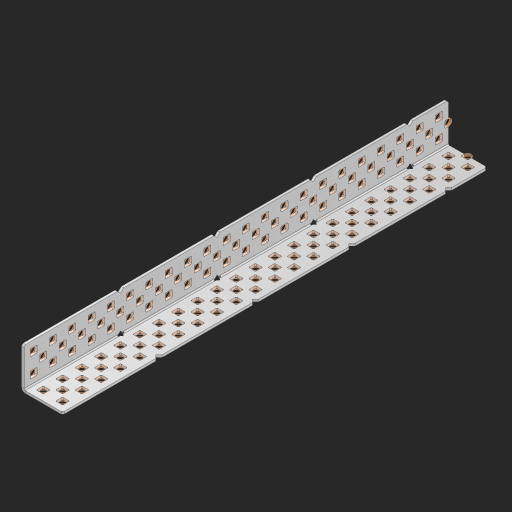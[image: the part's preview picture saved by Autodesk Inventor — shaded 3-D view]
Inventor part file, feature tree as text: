
AUTODESK INVENTOR PART (.ipt)
format: ipt  version: 2023 (Build 270158000, 158)  size: 1,655,808 bytes
history: native  units: in
note: dims shown in document units (in); Inventor stores cm internally (conversion verified against a paired STEP export)
features: other x138, extrude x130, sheet_metal_op x8, sketch x7, pattern_linear x2, mirror x1, chamfer x1
ambient origin geometry x8: Origin, YZ Plane, XZ Plane, XY Plane, X Axis, Y Axis, Z Axis, Center Point
bodies: Solid1 (feature_tree), Body (feature_tree)
feature tree (287):
  sheet_metal_op  "Flanges"
  sheet_metal_op  "Body Pattern"
  pattern_linear  "Center Pattern"  Spacing1=1.0in  [1 undecoded]
  other  "Arc Length"
  pattern_linear  "Notch Pattern"  Spacing1=0.25in  [1 undecoded]
  other  "Diagonal Plane"
  mirror  "Everything Mirrored"
  chamfer  "End Chamfer"
  sketch  "Sketch1"  dims[d0=1.0in]
  other  "Plate1"
  sketch  "Sketch2"  dims[d1=11.0in]
  other  "Plate2"
  sheet_metal_op  "Bend1"
  sheet_metal_op  "Corner1"
  sketch  "Sketch8"  dims[d2=0.0625in]
  sketch  "Sketch9"  dims[d3=0.0625in]
  other  "Srf91"
  sheet_metal_op  "Body Pattern Sketch"
  other  "Srf92"
  sketch  "Sketch13"  dims[d4=0.0312in]
  sketch  "Sketch15"  dims[d5=0.125in]
  sketch  "Sketch16"  dims[d6=0.0625in d7=1.0in d8=90.0deg d9=0.0312in d10=0.25in d11=0.0625in d12=0.0625in d49=0.182in d50=0.02in d52=0.25in d53=0.0625in d54=0.0in d55=0.172in d56=1.0in d57=0.0in d60=8.6614in d62=0.5in d63=0.7874in d65=0.5in d85=0.1473in d86=0.1782in d89=0.0625in d90=0.0in d91=0.04in d92=0.0491in d95=2.5in d96=0.04in d97=0.25in d98=45.0deg d99=0.25in d106=0.182in d107=0.02in d108=0.5in d110=0.0625in d111=0.0in d112=0.172in d113=0.5in d114=0.0in d117=0.5in d123=0.25in d125=0.25in d126=0.0491in d127=0.1473in d128=0.08in d129=0.04in d130=2.5in]
  other  "Srf786"
  other  "Srf856"
  other  "Srf857"
  other  "Srf858"
  other  "Srf859"
  other  "Srf860"
  other  "Srf861"
  other  "Srf889"
  other  "Srf890"
  other  "Srf891"
  other  "Srf1275"
  other  "Srf1276"
  other  "Srf1278"
  other  "Srf1279"
  other  "Srf1280"
  other  "Srf1281"
  other  "Srf1282"
  other  "Srf1283"
  other  "Srf1277"
  other  "Srf1285"
  other  "Srf1286"
  other  "Srf1287"
  other  "Srf1383"
  other  "Srf1384"
  other  "Srf1385"
  other  "Srf1386"
  other  "Srf1387"
  other  "Srf1388"
  other  "Srf1389"
  other  "Srf1390"
  other  "Srf1391"
  other  "Srf1392"
  other  "Srf1393"
  other  "Srf1394"
  other  "Srf1395"
  other  "Srf1396"
  other  "Srf1397"
  other  "Srf1398"
  other  "Srf1399"
  other  "Srf1400"
  other  "Srf1401"
  other  "Srf1402"
  other  "Srf1403"
  other  "Srf1404"
  other  "Srf1405"
  other  "Srf1406"
  other  "Srf1407"
  other  "Srf1408"
  other  "Srf1409"
  other  "Srf1410"
  other  "Srf1411"
  other  "Srf1412"
  other  "Srf1413"
  other  "Srf1414"
  other  "Srf1415"
  other  "Srf1416"
  other  "Srf1417"
  other  "Srf1418"
  other  "Srf1445"
  other  "Srf1446"
  other  "Srf1447"
  other  "Srf1448"
  other  "Srf1449"
  other  "Srf1450"
  other  "Srf1451"
  other  "Srf1452"
  other  "Srf1453"
  other  "Srf1454"
  other  "Srf1455"
  other  "Srf1456"
  other  "Srf1457"
  other  "Srf1458"
  other  "Srf1459"
  other  "Srf1460"
  other  "Srf1461"
  other  "Srf1462"
  other  "Srf1475"
  other  "Srf1476"
  other  "Srf1477"
  other  "Srf1478"
  other  "Srf1479"
  other  "Srf1480"
  other  "Srf1481"
  other  "Srf1482"
  other  "Srf1483"
  other  "Srf1484"
  other  "Srf1485"
  other  "Srf1486"
  other  "Srf1487"
  other  "Srf1488"
  other  "Srf1489"
  other  "Srf1490"
  other  "Srf1491"
  other  "Srf1492"
  other  "Srf1493"
  other  "Srf1494"
  other  "Srf1495"
  other  "Srf1496"
  other  "Srf1497"
  other  "Srf1498"
  other  "Srf1499"
  other  "Srf1500"
  other  "Srf1501"
  other  "Srf1502"
  other  "Srf1503"
  other  "Srf1504"
  other  "Srf1505"
  other  "Srf1506"
  other  "Srf1507"
  other  "Srf1508"
  other  "Srf1509"
  other  "Srf1510"
  other  "Srf1537"
  other  "Srf1538"
  other  "Srf1539"
  other  "Srf1540"
  other  "Srf1541"
  other  "Srf1542"
  other  "Srf1543"
  other  "Srf1544"
  other  "Srf1545"
  other  "Srf1546"
  other  "Srf1547"
  other  "Srf1548"
  other  "Srf1549"
  other  "Srf1550"
  other  "Srf1551"
  other  "Srf1552"
  other  "Srf1553"
  other  "Srf1554"
  sheet_metal_op  "Body Stamp"
  sheet_metal_op  "Body Circle"
  other  "Center Stamp"
  other  "Center Circle"
  sheet_metal_op  "Notch"
  extrude  "ExtrusionSrf92"  Depth=0.0625in
  extrude  "ExtrusionSrf856"  Depth=0.0625in
  extrude  "ExtrusionSrf857"  Depth=0.182in
  extrude  "ExtrusionSrf858"  Depth=0.02in
  extrude  "ExtrusionSrf859"  Depth=0.25in
  extrude  "ExtrusionSrf860"  Depth=0.0625in
  extrude  "ExtrusionSrf861"  TaperAngle=0.0deg  [1 undecoded]
  extrude  "ExtrusionSrf889"  Depth=2.5in
  extrude  "ExtrusionSrf890"  Depth=1.0in TaperAngle=0.0deg
  extrude  "ExtrusionSrf891"  Depth=2.5in
  extrude  "ExtrusionSrf1275"  Depth=0.5in
  extrude  "ExtrusionSrf1276"  Depth=2.5in
  extrude  "ExtrusionSrf1277"  Depth=2.5in
  extrude  "ExtrusionSrf1278"  Depth=0.0625in
  extrude  "ExtrusionSrf1279"  Depth=2.5in TaperAngle=0.0deg
  extrude  "ExtrusionSrf1280"  Depth=2.5in
  extrude  "ExtrusionSrf1281"  Depth=0.25in TaperAngle=45.0deg
  extrude  "ExtrusionSrf1282"  Depth=0.25in
  extrude  "ExtrusionSrf1345"  Depth=0.182in
  extrude  "ExtrusionSrf1346"  Depth=0.02in
  extrude  "ExtrusionSrf1347"  Depth=0.5in
  extrude  "ExtrusionSrf1348"  Depth=0.0625in
  extrude  "ExtrusionSrf1383"  TaperAngle=0.0deg  [1 undecoded]
  extrude  "ExtrusionSrf1384"  Depth=2.5in
  extrude  "ExtrusionSrf1385"  Depth=0.5in TaperAngle=0.0deg
  extrude  "ExtrusionSrf1386"  Depth=0.5in
  extrude  "ExtrusionSrf1387"  Depth=0.25in
  extrude  "ExtrusionSrf1388"  Depth=0.25in
  extrude  "ExtrusionSrf1389"  Depth=2.5in
  extrude  "ExtrusionSrf1390"  Depth=2.5in
  extrude  "ExtrusionSrf1391"  Depth=2.5in
  extrude  "ExtrusionSrf1392"  Depth=2.5in
  extrude  "ExtrusionSrf1393"  Depth=2.5in
  extrude  "ExtrusionSrf1394"  [1 undecoded]
  extrude  "ExtrusionSrf1395"  [1 undecoded]
  extrude  "ExtrusionSrf1396"  [1 undecoded]
  extrude  "ExtrusionSrf1397"  [1 undecoded]
  extrude  "ExtrusionSrf1398"  [1 undecoded]
  extrude  "ExtrusionSrf1399"  [1 undecoded]
  extrude  "ExtrusionSrf1400"  [1 undecoded]
  extrude  "ExtrusionSrf1401"  [1 undecoded]
  extrude  "ExtrusionSrf1402"  [1 undecoded]
  extrude  "ExtrusionSrf1403"  [1 undecoded]
  extrude  "ExtrusionSrf1404"  [1 undecoded]
  extrude  "ExtrusionSrf1405"  [1 undecoded]
  extrude  "ExtrusionSrf1406"  [1 undecoded]
  extrude  "ExtrusionSrf1407"  [1 undecoded]
  extrude  "ExtrusionSrf1408"  [1 undecoded]
  extrude  "ExtrusionSrf1409"  [1 undecoded]
  extrude  "ExtrusionSrf1410"  [1 undecoded]
  extrude  "ExtrusionSrf1411"  [1 undecoded]
  extrude  "ExtrusionSrf1412"  [1 undecoded]
  extrude  "ExtrusionSrf1413"  [1 undecoded]
  extrude  "ExtrusionSrf1414"  [1 undecoded]
  extrude  "ExtrusionSrf1415"  [1 undecoded]
  extrude  "ExtrusionSrf1416"  [1 undecoded]
  extrude  "ExtrusionSrf1417"  [1 undecoded]
  extrude  "ExtrusionSrf1418"  [1 undecoded]
  extrude  "ExtrusionSrf1445"  [1 undecoded]
  extrude  "ExtrusionSrf1446"  [1 undecoded]
  extrude  "ExtrusionSrf1447"  [1 undecoded]
  extrude  "ExtrusionSrf1448"  [1 undecoded]
  extrude  "ExtrusionSrf1449"  [1 undecoded]
  extrude  "ExtrusionSrf1450"  [1 undecoded]
  extrude  "ExtrusionSrf1451"  [1 undecoded]
  extrude  "ExtrusionSrf1452"  [1 undecoded]
  extrude  "ExtrusionSrf1453"  [1 undecoded]
  extrude  "ExtrusionSrf1454"  [1 undecoded]
  extrude  "ExtrusionSrf1455"  [1 undecoded]
  extrude  "ExtrusionSrf1456"  [1 undecoded]
  extrude  "ExtrusionSrf1457"  [1 undecoded]
  extrude  "ExtrusionSrf1458"  [1 undecoded]
  extrude  "ExtrusionSrf1459"  [1 undecoded]
  extrude  "ExtrusionSrf1460"  [1 undecoded]
  extrude  "ExtrusionSrf1461"  [1 undecoded]
  extrude  "ExtrusionSrf1462"  [1 undecoded]
  extrude  "ExtrusionSrf1475"  [1 undecoded]
  extrude  "ExtrusionSrf1476"  [1 undecoded]
  extrude  "ExtrusionSrf1477"  [1 undecoded]
  extrude  "ExtrusionSrf1478"  [1 undecoded]
  extrude  "ExtrusionSrf1479"  [1 undecoded]
  extrude  "ExtrusionSrf1480"  [1 undecoded]
  extrude  "ExtrusionSrf1481"  [1 undecoded]
  extrude  "ExtrusionSrf1482"  [1 undecoded]
  extrude  "ExtrusionSrf1483"  [1 undecoded]
  extrude  "ExtrusionSrf1484"  [1 undecoded]
  extrude  "ExtrusionSrf1485"  [1 undecoded]
  extrude  "ExtrusionSrf1486"  [1 undecoded]
  extrude  "ExtrusionSrf1487"  [1 undecoded]
  extrude  "ExtrusionSrf1488"  [1 undecoded]
  extrude  "ExtrusionSrf1489"  [1 undecoded]
  extrude  "ExtrusionSrf1490"  [1 undecoded]
  extrude  "ExtrusionSrf1491"  [1 undecoded]
  extrude  "ExtrusionSrf1492"  [1 undecoded]
  extrude  "ExtrusionSrf1493"  [1 undecoded]
  extrude  "ExtrusionSrf1494"  [1 undecoded]
  extrude  "ExtrusionSrf1495"  [1 undecoded]
  extrude  "ExtrusionSrf1496"  [1 undecoded]
  extrude  "ExtrusionSrf1497"  [1 undecoded]
  extrude  "ExtrusionSrf1498"  [1 undecoded]
  extrude  "ExtrusionSrf1499"  [1 undecoded]
  extrude  "ExtrusionSrf1500"  [1 undecoded]
  extrude  "ExtrusionSrf1501"  [1 undecoded]
  extrude  "ExtrusionSrf1502"  [1 undecoded]
  extrude  "ExtrusionSrf1503"  [1 undecoded]
  extrude  "ExtrusionSrf1504"  [1 undecoded]
  extrude  "ExtrusionSrf1505"  [1 undecoded]
  extrude  "ExtrusionSrf1506"  [1 undecoded]
  extrude  "ExtrusionSrf1507"  [1 undecoded]
  extrude  "ExtrusionSrf1508"  [1 undecoded]
  extrude  "ExtrusionSrf1509"  [1 undecoded]
  extrude  "ExtrusionSrf1510"  [1 undecoded]
  extrude  "ExtrusionSrf1537"  [1 undecoded]
  extrude  "ExtrusionSrf1538"  [1 undecoded]
  extrude  "ExtrusionSrf1539"  [1 undecoded]
  extrude  "ExtrusionSrf1540"  [1 undecoded]
  extrude  "ExtrusionSrf1541"  [1 undecoded]
  extrude  "ExtrusionSrf1542"  [1 undecoded]
  extrude  "ExtrusionSrf1543"  [1 undecoded]
  extrude  "ExtrusionSrf1544"  [1 undecoded]
  extrude  "ExtrusionSrf1545"  [1 undecoded]
  extrude  "ExtrusionSrf1546"  [1 undecoded]
  extrude  "ExtrusionSrf1547"  [1 undecoded]
  extrude  "ExtrusionSrf1548"  [1 undecoded]
  extrude  "ExtrusionSrf1549"  [1 undecoded]
  extrude  "ExtrusionSrf1550"  [1 undecoded]
  extrude  "ExtrusionSrf1551"  [1 undecoded]
  extrude  "ExtrusionSrf1552"  [1 undecoded]
  extrude  "ExtrusionSrf1553"  [1 undecoded]
  extrude  "ExtrusionSrf1554"  [1 undecoded]
note: 101 required parameter values undecoded (feature->parameter linkage not recoverable at this tier; creation-order binding heuristic only, values carry confidence <= 0.55)
